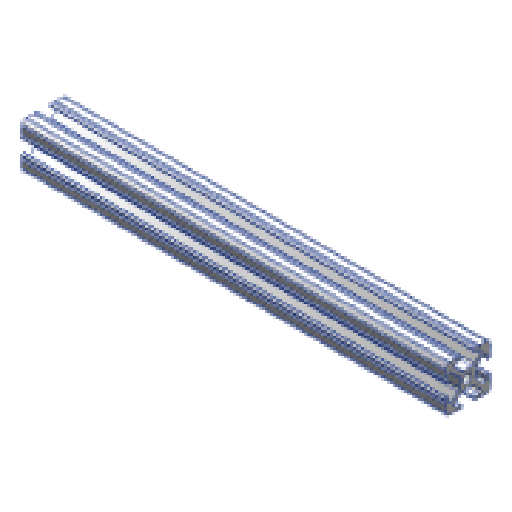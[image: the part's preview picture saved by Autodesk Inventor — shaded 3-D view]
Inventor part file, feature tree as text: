
AUTODESK INVENTOR PART (.ipt)
format: ipt  version: 2025 (Build 290162000, 162)  size: 246,272 bytes
history: native  units: in
note: dims shown in document units (in); Inventor stores cm internally (conversion verified against a paired STEP export)
features: extrude x1, sketch x1
ambient origin geometry x8: Origin, YZ Plane, XZ Plane, XY Plane, X Axis, Y Axis, Z Axis, Center Point
bodies: Solid1 (feature_tree)
feature tree (2):
  extrude  "Extrusion1"  [1 undecoded]
  sketch  "Sketch1"  dims[d0=9.2126in d1=0.0in]
note: 1 required parameter value undecoded (feature->parameter linkage not recoverable at this tier; creation-order binding heuristic only, values carry confidence <= 0.55)
